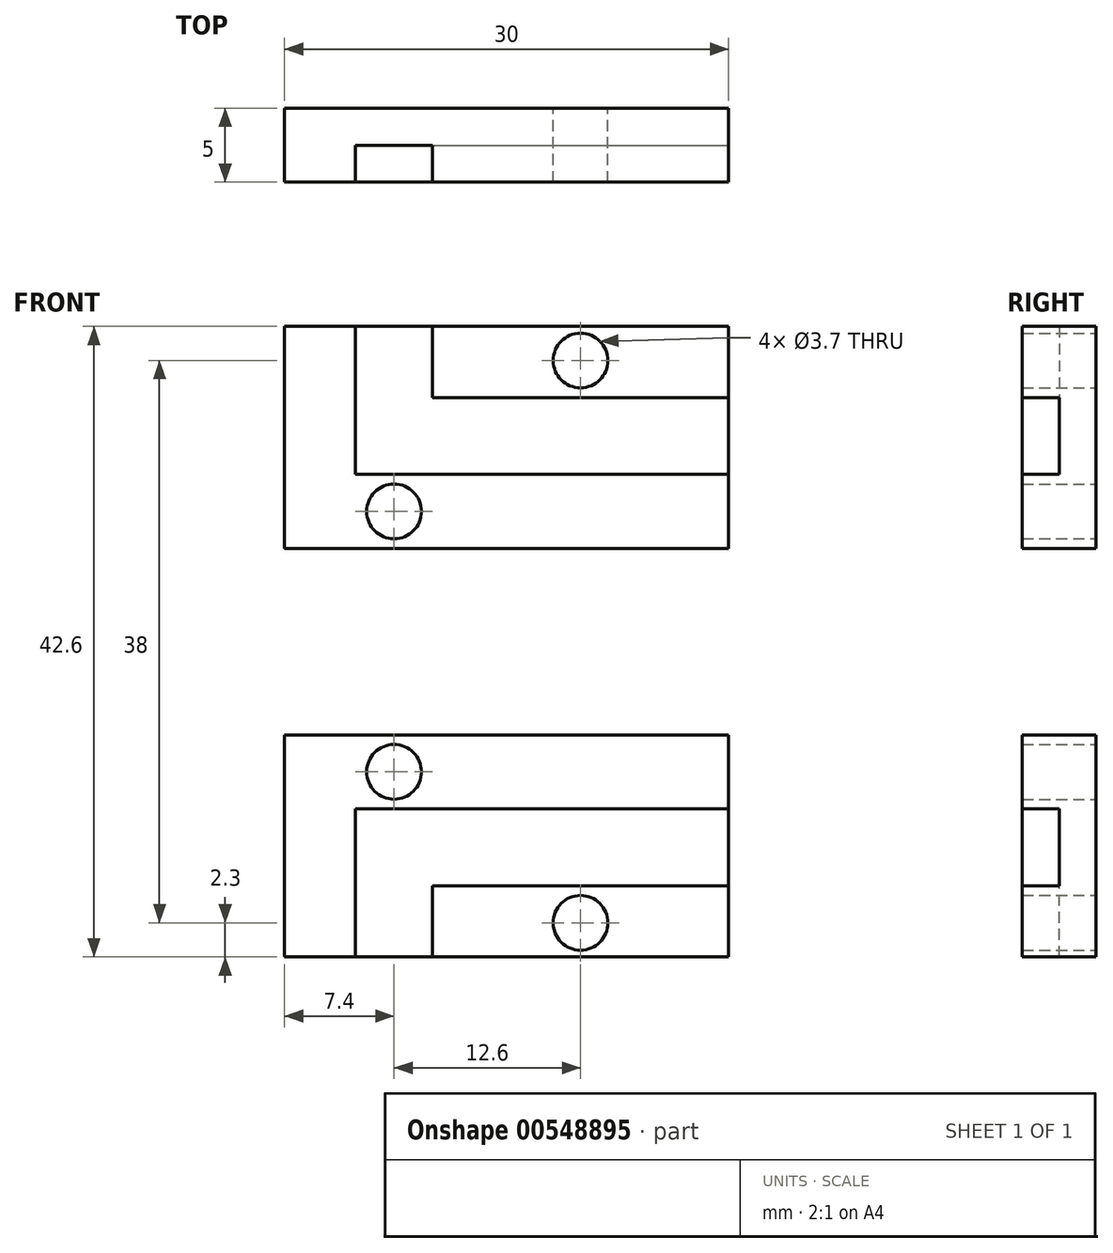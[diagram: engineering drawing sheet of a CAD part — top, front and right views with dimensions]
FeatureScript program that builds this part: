
annotation { "Feature Type Name" : "Feature", "Feature Type Description" : "" }
export const myFeature = defineFeature(function(context is Context, id is Id, definition is map)
    precondition{}
    {
        {
            var Q0;
            Q0=qCreatedBy(makeId("Front.planeOp"),FACE);
            var sketch = newSketch(context, id + "F0", { "sketchPlane" : qUnion([Q0])});
            skLineSegment(sketch, "E0.bottom", {"start": v(-15, 7.5) * mm, "end": v(15, 7.5) * mm});
            skLineSegment(sketch, "E0.top", {"start": v(-15, -7.5) * mm, "end": v(15, -7.5) * mm});
            skLineSegment(sketch, "E0.left", {"start": v(-15, 7.5) * mm, "end": v(-15, -7.5) * mm});
            skLineSegment(sketch, "E0.right", {"start": v(15, 7.5) * mm, "end": v(15, -7.5) * mm});
            skPoint(sketch, "E0.middle", {"position": v(0, 0) * mm});
            skLineSegment(sketch, "E1.bottom", {"start": v(15, -2.5) * mm, "end": v(-5, -2.5) * mm});
            skLineSegment(sketch, "E1.top", {"start": v(15, 2.7) * mm, "end": v(-5, 2.7) * mm});
            skLineSegment(sketch, "E1.left", {"start": v(15, -2.5) * mm, "end": v(15, 2.7) * mm});
            skLineSegment(sketch, "E2.bottom", {"start": v(-5, -2.5) * mm, "end": v(-10.2, -2.5) * mm});
            skLineSegment(sketch, "E2.top", {"start": v(-5, 7.5) * mm, "end": v(-10.2, 7.5) * mm});
            skLineSegment(sketch, "E2.left", {"start": v(-5, 2.7) * mm, "end": v(-5, 7.5) * mm});
            skLineSegment(sketch, "E2.right", {"start": v(-10.2, -2.5) * mm, "end": v(-10.2, 7.5) * mm});
            skCircle(sketch, "E3", {"center": v(5, 5.2) * mm, "radius": 1.85 * mm});
            skPoint(sketch, "E3.centerSnap0", {"position": v(5, 2.7) * mm});
            skCircle(sketch, "E4", {"center": v(-7.6, -5) * mm, "radius": 1.85 * mm});
            skPoint(sketch, "E4.centerSnap0", {"position": v(-7.6, -2.5) * mm});
            skSolve(sketch);
        }
        {
            var Q0;
            {var subQ0=sQuery(id+"F0.wireOp",EDGE,"E1.top");Q0=makeQuery(id+"F0.imprint","IMPRINT",FACE,{"disambiguationData":[TD([[makeQuery(id+"F0.imprint","IMPRINT",EDGE,{"derivedFrom":subQ0}),-1.0]])]});}
            var Q1;
            Q1=makeQuery(id+"F0.imprint","IMPRINT",FACE,{"disambiguationData":[TD([[makeQuery(id+"F0.imprint","IMPRINT",EDGE,{"derivedFrom":sQuery(id+"F0.wireOp",EDGE,"E1.bottom")}),-1.0]])]});
            var Q2;
            {var subQ1=sQuery(id+"F0.wireOp",EDGE,"E0.top");Q2=makeQuery(id+"F0.imprint","IMPRINT",FACE,{"disambiguationData":[TD([[makeQuery(id+"F0.imprint","IMPRINT",EDGE,{"derivedFrom":subQ1}),1.0]])]});}
            extrude(context, id + "F1", {"entities" : qUnion([Q0, Q1, Q2]), "depth" : 2.5 * mm, "offsetDistance" : 25 * mm});
        }
        {
            var Q0;
            {var subQ0=sQuery(id+"F0.wireOp",EDGE,"E1.top");Q0=makeQuery(id+"F0.imprint","IMPRINT",FACE,{"disambiguationData":[TD([[makeQuery(id+"F0.imprint","IMPRINT",EDGE,{"derivedFrom":subQ0}),-1.0]])]});}
            var Q1;
            {var subQ1=sQuery(id+"F0.wireOp",EDGE,"E0.top");Q1=makeQuery(id+"F0.imprint","IMPRINT",FACE,{"disambiguationData":[TD([[makeQuery(id+"F0.imprint","IMPRINT",EDGE,{"derivedFrom":subQ1}),1.0]])]});}
            extrude(context, id + "F2", {"entities" : qUnion([Q0, Q1]), "operationType" : NewBodyOperationType.ADD, "depth" : 5 * mm, "offsetDistance" : 25 * mm});
        }
        {
            var Q0;
            Q0=makeQuery(id+"F1.opExtrude","SWEPT_BODY",BODY,{"disambiguationData":[OSD([sQuery(id+"F0.wireOp",EDGE,"E0.bottom"),sQuery(id+"F0.wireOp",EDGE,"E0.top"),sQuery(id+"F0.wireOp",EDGE,"E0.left"),sQuery(id+"F0.wireOp",EDGE,"E0.right"),sQuery(id+"F0.wireOp",EDGE,"E1.left"),sQuery(id+"F0.wireOp",EDGE,"E2.top"),sQuery(id+"F0.wireOp",EDGE,"E3"),sQuery(id+"F0.wireOp",EDGE,"E4")])]});
            var Q1;
            Q1=makeQuery(id+"F2.opExtrude","CAP_EDGE",EDGE,{"disambiguationData":[OSD([sQuery(id+"F0.wireOp",EDGE,"E2.right")])],"isStart":false});
            transform(context, id + "F3", {"entities" : qUnion([Q0]), "transformType" : TransformType.TRANSLATION_DISTANCE, "transformDirection" : qUnion([Q1]), "distance" : 13.8 * mm, "makeCopy" : false});
        }
        {
            var Q0;
            Q0=makeQuery(id+"F1.opExtrude","SWEPT_BODY",BODY,{"disambiguationData":[OSD([sQuery(id+"F0.wireOp",EDGE,"E0.bottom"),sQuery(id+"F0.wireOp",EDGE,"E0.top"),sQuery(id+"F0.wireOp",EDGE,"E0.left"),sQuery(id+"F0.wireOp",EDGE,"E0.right"),sQuery(id+"F0.wireOp",EDGE,"E1.left"),sQuery(id+"F0.wireOp",EDGE,"E2.top"),sQuery(id+"F0.wireOp",EDGE,"E3"),sQuery(id+"F0.wireOp",EDGE,"E4")])]});
            var Q1;
            Q1=qCreatedBy(makeId("Top.planeOp"),FACE);
            mirror(context, id + "F4", {"entities" : qUnion([Q0]), "mirrorPlane" : qUnion([Q1])});
        }
    });
